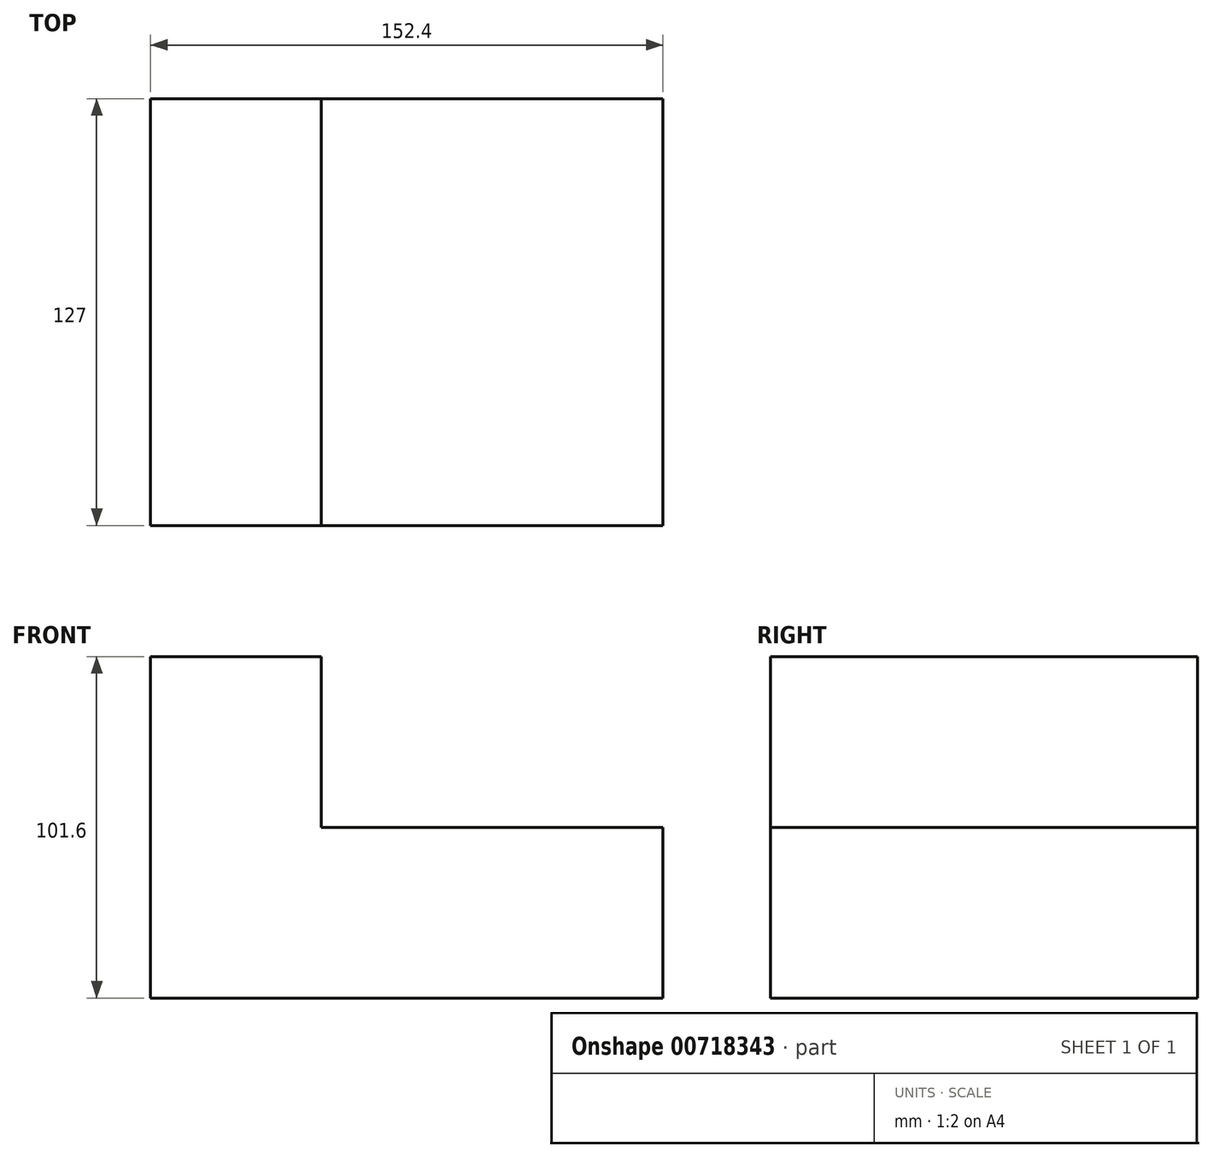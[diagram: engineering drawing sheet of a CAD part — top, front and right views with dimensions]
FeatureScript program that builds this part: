
annotation { "Feature Type Name" : "Feature", "Feature Type Description" : "" }
export const myFeature = defineFeature(function(context is Context, id is Id, definition is map)
    precondition{}
    {
        {
            var Q0;
            Q0=qCreatedBy(makeId("Front.planeOp"),FACE);
            var sketch = newSketch(context, id + "F0", { "sketchPlane" : qUnion([Q0])});
            skLineSegment(sketch, "E0", {"start": v(0, 0) * mm, "end": v(152.4, 0) * mm});
            skLineSegment(sketch, "E1", {"start": v(152.4, 0) * mm, "end": v(152.4, 50.8) * mm});
            skLineSegment(sketch, "E2", {"start": v(152.4, 50.8) * mm, "end": v(50.8, 50.8) * mm});
            skLineSegment(sketch, "E3", {"start": v(50.8, 50.8) * mm, "end": v(50.8, 101.6) * mm});
            skLineSegment(sketch, "E4", {"start": v(50.8, 101.6) * mm, "end": v(0, 101.6) * mm});
            skLineSegment(sketch, "E5", {"start": v(0, 101.6) * mm, "end": v(0, 0) * mm});
            skSolve(sketch);
        }
        {
            var Q0;
            Q0=makeQuery(id+"F0.imprint","IMPRINT",FACE,{"disambiguationData":[TD([[makeQuery(id+"F0.imprint","IMPRINT",EDGE,{"derivedFrom":sQuery(id+"F0.wireOp",EDGE,"E0")}),1.0]])]});
            extrude(context, id + "F1", {"entities" : qUnion([Q0]), "oppositeDirection" : true, "depth" : 127 * mm, "offsetDistance" : 25.4 * mm});
        }
    });
